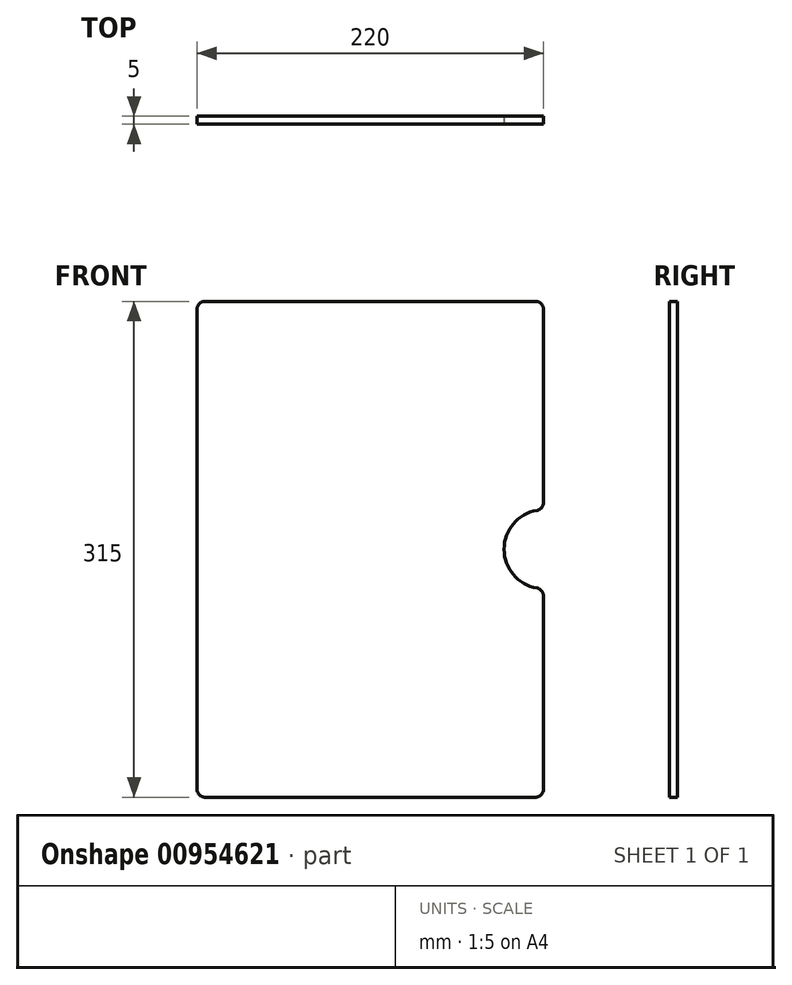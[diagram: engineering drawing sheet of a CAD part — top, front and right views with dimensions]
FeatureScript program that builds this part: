
annotation { "Feature Type Name" : "Feature", "Feature Type Description" : "" }
export const myFeature = defineFeature(function(context is Context, id is Id, definition is map)
    precondition{}
    {
        {
            var Q0;
            Q0=qCreatedBy(makeId("Front.planeOp"),FACE);
            var sketch = newSketch(context, id + "F0", { "sketchPlane" : qUnion([Q0])});
            skLineSegment(sketch, "E0.bottom", {"start": v(110, 157.5) * mm, "end": v(-110, 157.5) * mm});
            skLineSegment(sketch, "E0.top", {"start": v(110, -157.5) * mm, "end": v(-110, -157.5) * mm});
            skLineSegment(sketch, "E0.left", {"start": v(110, 157.5) * mm, "end": v(110, -157.5) * mm});
            skLineSegment(sketch, "E0.right", {"start": v(-110, 157.5) * mm, "end": v(-110, -157.5) * mm});
            skPoint(sketch, "E0.middle", {"position": v(0, 0) * mm});
            skSolve(sketch);
        }
        {
            var Q0;
            Q0 = qSketchRegion(id + "F0", true);
            extrude(context, id + "F1", {"entities" : qUnion([Q0]), "depth" : 5 * mm, "offsetDistance" : 25 * mm});
        }
        {
            var Q0;
            Q0=makeQuery(id+"F1.opExtrude","CAP_FACE",FACE,{"disambiguationData":[OSD([sQuery(id+"F0.wireOp",EDGE,"E0.bottom"),sQuery(id+"F0.wireOp",EDGE,"E0.top"),sQuery(id+"F0.wireOp",EDGE,"E0.left"),sQuery(id+"F0.wireOp",EDGE,"E0.right")])],"isStart":false});
            var sketch = newSketch(context, id + "F2", { "sketchPlane" : qUnion([Q0])});
            skCircle(sketch, "E1", {"center": v(110, 0) * mm, "radius": 25 * mm});
            skSolve(sketch);
        }
        {
            var Q0;
            Q0 = qSketchRegion(id + "F2", true);
            extrude(context, id + "F3", {"entities" : qUnion([Q0]), "operationType" : NewBodyOperationType.REMOVE, "oppositeDirection" : true, "depth" : 25 * mm, "offsetDistance" : 25 * mm});
        }
        {
            var Q0;
            Q0=makeQuery(id+"F3.boolean.opBoolean","INTERSECT",EDGE,{"disambiguationData":[OD(1.0)],"derivedFrom":[makeQuery(id+"F1.opExtrude","SWEPT_FACE",FACE,{"disambiguationData":[OSD([sQuery(id+"F0.wireOp",EDGE,"E0.left")])]}),makeQuery(id+"F3.opExtrude","SWEPT_FACE",FACE,{"disambiguationData":[OSD([sQuery(id+"F2.wireOp",EDGE,"E1")])]})]});
            var Q1;
            Q1=makeQuery(id+"F3.boolean.opBoolean","INTERSECT",EDGE,{"disambiguationData":[OD(0.0)],"derivedFrom":[makeQuery(id+"F1.opExtrude","SWEPT_FACE",FACE,{"disambiguationData":[OSD([sQuery(id+"F0.wireOp",EDGE,"E0.left")])]}),makeQuery(id+"F3.opExtrude","SWEPT_FACE",FACE,{"disambiguationData":[OSD([sQuery(id+"F2.wireOp",EDGE,"E1")])]})]});
            var Q2;
            Q2=makeQuery(id+"F1.opExtrude","SWEPT_EDGE",EDGE,{"disambiguationData":[OSD([sQuery(id+"F0.wireOp",EDGE,"E0.bottom"),sQuery(id+"F0.wireOp",EDGE,"E0.left")])]});
            var Q3;
            Q3=makeQuery(id+"F1.opExtrude","SWEPT_EDGE",EDGE,{"disambiguationData":[OSD([sQuery(id+"F0.wireOp",EDGE,"E0.bottom"),sQuery(id+"F0.wireOp",EDGE,"E0.right")])]});
            var Q4;
            Q4=makeQuery(id+"F1.opExtrude","SWEPT_EDGE",EDGE,{"disambiguationData":[OSD([sQuery(id+"F0.wireOp",EDGE,"E0.top"),sQuery(id+"F0.wireOp",EDGE,"E0.right")])]});
            var Q5;
            Q5=makeQuery(id+"F1.opExtrude","SWEPT_EDGE",EDGE,{"disambiguationData":[OSD([sQuery(id+"F0.wireOp",EDGE,"E0.top"),sQuery(id+"F0.wireOp",EDGE,"E0.left")])]});
            fillet(context, id + "F4", {"entities" : qUnion([Q0, Q1, Q2, Q3, Q4, Q5]), "radius" : 5 * mm, "tangentPropagation" : true, "allowEdgeOverflow" : false});
        }
    });
